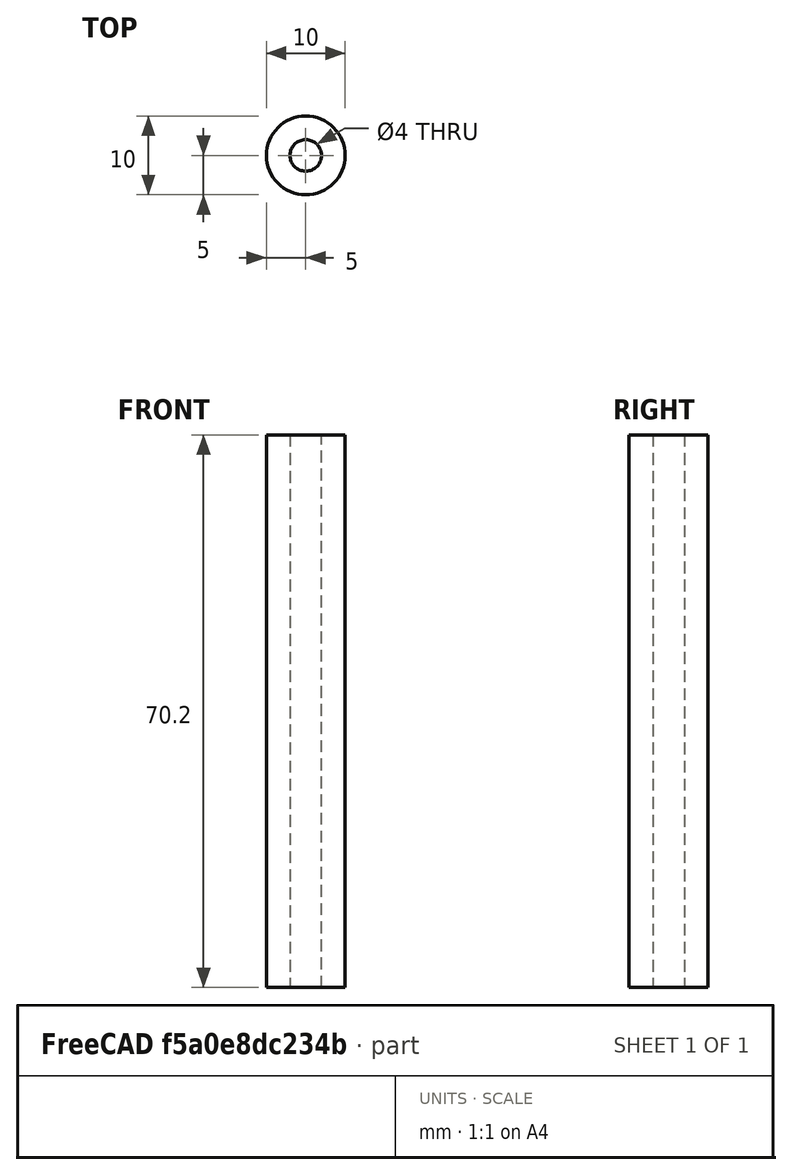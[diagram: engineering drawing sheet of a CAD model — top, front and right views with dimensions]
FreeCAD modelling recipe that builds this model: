
FCSTD DOCUMENT  (FreeCAD 0.20R29410 (Git))
Label: #12_MotorsBaseSpacer
License: All rights reserved
LicenseURL: http://en.wikipedia.org/wiki/All_rights_reserved
objects: Sketcher::SketchObject×1, PartDesign::Pad×1, PartDesign::Body×1
note: 4 computed .brp shape members not serialized (recipe doc carries the construction recipe); baked Part::Feature solids carry a one-line shape summary decoded from their .brp

FEATURE [Sketcher::SketchObject] Sketch
  FullyConstrained = true
  MapMode = 5
  Support = -> [XY_Plane]
  sketch-geometry (2):
    g0: Circle CenterX=0 CenterY=0 CenterZ=0 NormalX=0 NormalY=0 NormalZ=1 AngleXU=0 Radius=5
    g1: Circle CenterX=0 CenterY=0 CenterZ=0 NormalX=0 NormalY=0 NormalZ=1 AngleXU=0 Radius=2
  constraints (4):
    c: Coincident(g0,g-1)
    c: Coincident(g1,g0)
    c: Diameter(g1) = 4
    c: Diameter(g0) = 10
FEATURE [PartDesign::Pad] Pad
  Direction = (0,0,1)
  Length = 70.2
  Length2 = 10
  Profile = -> Sketch
  ReferenceAxis = -> Sketch [N_Axis]
  Type = 0
FEATURE [PartDesign::Body] Body
  Group = -> [Sketch,Pad]
  Origin = -> Origin
  Tip = -> Pad
